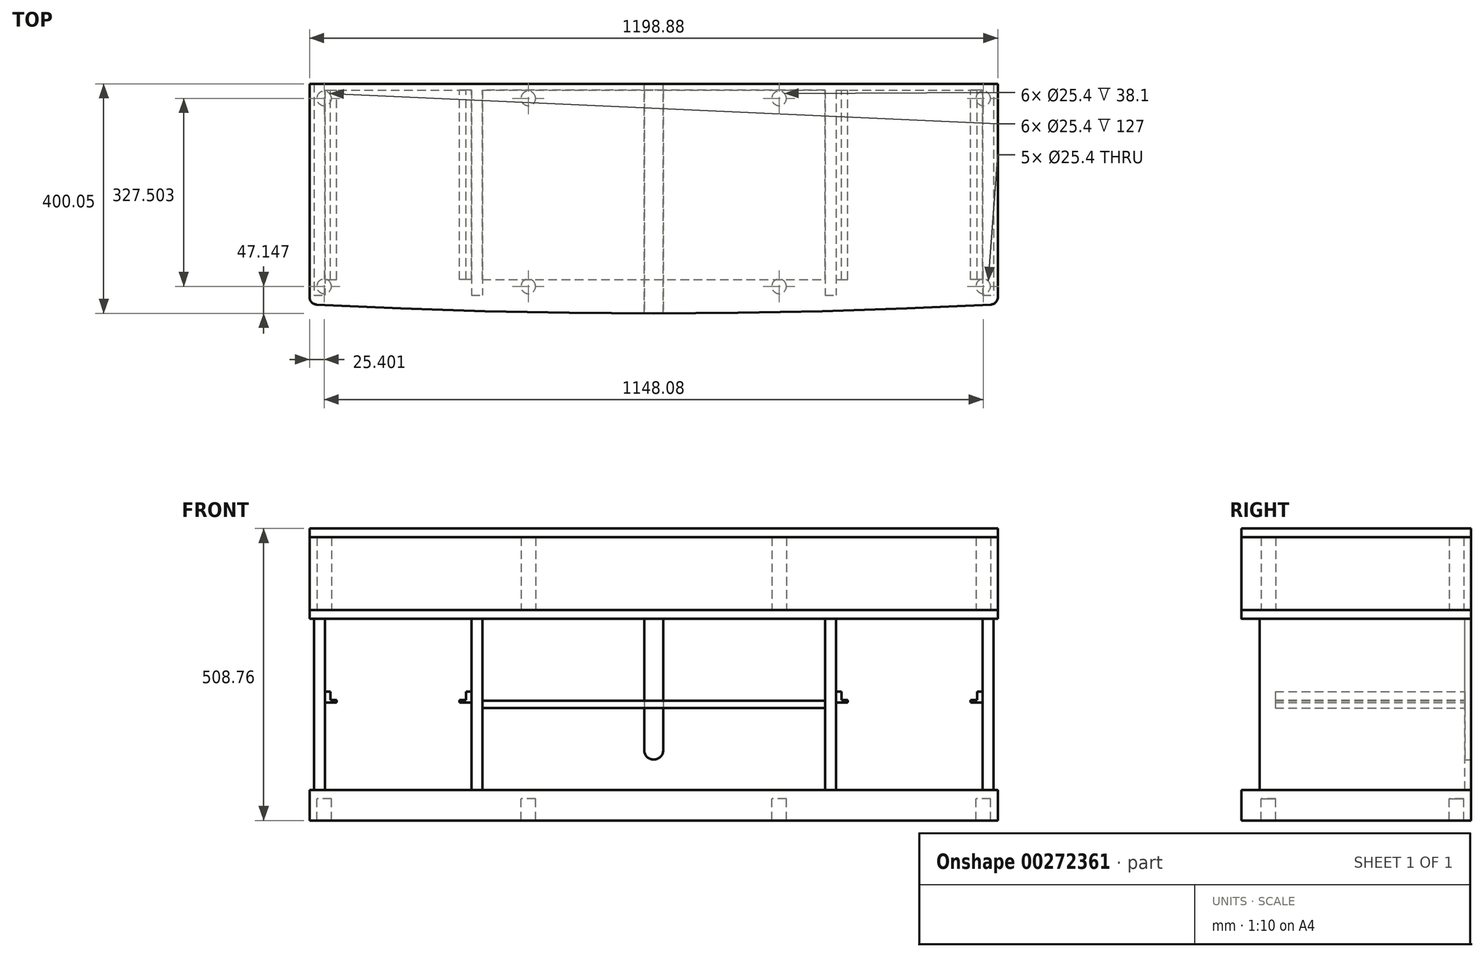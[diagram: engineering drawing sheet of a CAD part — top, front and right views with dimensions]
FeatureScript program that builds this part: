
annotation { "Feature Type Name" : "Feature", "Feature Type Description" : "" }
export const myFeature = defineFeature(function(context is Context, id is Id, definition is map)
    precondition{}
    {
        {
            var Q0;
            Q0=qCreatedBy(makeId("Top.planeOp"),FACE);
            var sketch = newSketch(context, id + "F0", { "sketchPlane" : qUnion([Q0])});
            skLineSegment(sketch, "E0.bottom", {"start": v(-605.75, 224.13) * mm, "end": v(593.13, 224.13) * mm});
            skLineSegment(sketch, "E0.left", {"start": v(-605.75, 224.13) * mm, "end": v(-605.75, -147.84) * mm});
            skLineSegment(sketch, "E0.right", {"start": v(593.13, 224.13) * mm, "end": v(593.13, -147.84) * mm});
            skLineSegment(sketch, "E1", {"start": v(-6.3, 224.13) * mm, "end": v(-6.3, -175.92) * mm, "construction": true});
            skPoint(sketch, "E2.orphan", {"position": v(593.13, -175.92) * mm});
            skPoint(sketch, "E3.orphan", {"position": v(-605.75, -175.92) * mm});
            skArc(sketch, "E4", {"start": v(-593.71, -160.52) * mm, "mid": v(-6.3, -175.92) * mm, "end": v(581.1, -160.52) * mm});
            skPoint(sketch, "E5.end.orphan", {"position": v(-592.37, -175.92) * mm});
            skPoint(sketch, "E6.MirrorCS.end.orphan", {"position": v(579.75, -175.92) * mm});
            skArc(sketch, "E7", {"start": v(-605.75, -147.84) * mm, "mid": v(-602.26, -156.58) * mm, "end": v(-593.71, -160.52) * mm});
            skPoint(sketch, "E8.orphan", {"position": v(-605.75, -159.88) * mm});
            skArc(sketch, "E9.MirrorCS", {"start": v(593.13, -147.84) * mm, "mid": v(589.64, -156.58) * mm, "end": v(581.1, -160.52) * mm});
            skPoint(sketch, "E10.orphan", {"position": v(593.13, -159.88) * mm});
            skSolve(sketch);
        }
        {
            var Q0;
            Q0=makeQuery(id+"F0.imprint","IMPRINT",FACE,{"disambiguationData":[TD([[makeQuery(id+"F0.imprint","IMPRINT",EDGE,{"derivedFrom":sQuery(id+"F0.wireOp",EDGE,"E0.bottom")}),-1.0]])]});
            extrude(context, id + "F1", {"entities" : qUnion([Q0]), "depth" : 15.24 * mm});
        }
        {
            var Q0;
            Q0=qCreatedBy(makeId("Top.planeOp"),FACE);
            cPlane(context, id + "F2", {"entities" : qUnion([Q0]), "cplaneType" : CPlaneType.OFFSET, "offset" : 63.5 * mm, "oppositeDirection" : true, "width" : 152.4 * mm, "height" : 152.4 * mm});
        }
        {
            var Q0;
            Q0=makeQuery(id+"F1.opExtrude","SWEPT_BODY",BODY,{"disambiguationData":[OSD([sQuery(id+"F0.wireOp",EDGE,"E0.bottom"),sQuery(id+"F0.wireOp",EDGE,"E0.left"),sQuery(id+"F0.wireOp",EDGE,"E0.right"),sQuery(id+"F0.wireOp",EDGE,"E4"),sQuery(id+"F0.wireOp",EDGE,"E7"),sQuery(id+"F0.wireOp",EDGE,"E9.MirrorCS")])]});
            var Q1;
            Q1=qCreatedBy(id+"F2.planeOp",FACE);
            mirror(context, id + "F3", {"entities" : qUnion([Q0]), "mirrorPlane" : qUnion([Q1])});
        }
        {
            var Q0;
            Q0=makeQuery(id+"F3.opPattern","COPY",FACE,{"derivedFrom":makeQuery(id+"F1.opExtrude","CAP_FACE",FACE,{"disambiguationData":[OSD([sQuery(id+"F0.wireOp",EDGE,"E0.bottom"),sQuery(id+"F0.wireOp",EDGE,"E0.left"),sQuery(id+"F0.wireOp",EDGE,"E0.right"),sQuery(id+"F0.wireOp",EDGE,"E4"),sQuery(id+"F0.wireOp",EDGE,"E7"),sQuery(id+"F0.wireOp",EDGE,"E9.MirrorCS")])],"isStart":true}),"instanceName":"1"});
            var sketch = newSketch(context, id + "F4", { "sketchPlane" : qUnion([Q0])});
            skCircle(sketch, "E11", {"center": v(-580.35, -128.77) * mm, "radius": 12.7 * mm});
            skCircle(sketch, "E12.MirrorC", {"center": v(567.73, -128.77) * mm, "radius": 12.7 * mm});
            skCircle(sketch, "E13.MirrorC", {"center": v(-580.35, 198.73) * mm, "radius": 12.7 * mm});
            skCircle(sketch, "E14.MirrorC", {"center": v(567.73, 198.73) * mm, "radius": 12.7 * mm});
            skLineSegment(sketch, "E15", {"start": v(-605.75, 38.15) * mm, "end": v(593.13, 38.15) * mm, "construction": true});
            skCircle(sketch, "E16", {"center": v(-224.75, 198.73) * mm, "radius": 12.7 * mm});
            skCircle(sketch, "E17.MirrorC", {"center": v(212.13, 198.73) * mm, "radius": 12.7 * mm});
            skCircle(sketch, "E18.MirrorC", {"center": v(212.13, -128.77) * mm, "radius": 12.7 * mm});
            skLineSegment(sketch, "E19", {"start": v(-580.35, -128.77) * mm, "end": v(567.73, -128.77) * mm, "construction": true});
            skLineSegment(sketch, "E20", {"start": v(-224.75, 198.73) * mm, "end": v(-224.75, -211.27) * mm, "construction": true});
            skLineSegment(sketch, "E21", {"start": v(212.13, 198.73) * mm, "end": v(212.13, -214.73) * mm, "construction": true});
            skCircle(sketch, "E22", {"center": v(-224.75, -128.77) * mm, "radius": 12.7 * mm});
            skSolve(sketch);
        }
        {
            var Q0;
            Q0=makeQuery(id+"F4.imprint","IMPRINT",FACE,{"disambiguationData":[TD([[makeQuery(id+"F4.imprint","IMPRINT",EDGE,{"derivedFrom":sQuery(id+"F4.wireOp",EDGE,"E11")}),1.0]])]});
            var Q1;
            Q1=makeQuery(id+"F4.imprint","IMPRINT",FACE,{"disambiguationData":[TD([[makeQuery(id+"F4.imprint","IMPRINT",EDGE,{"derivedFrom":sQuery(id+"F4.wireOp",EDGE,"E13.MirrorC")}),-1.0]])]});
            var Q2;
            Q2=makeQuery(id+"F4.imprint","IMPRINT",FACE,{"disambiguationData":[TD([[makeQuery(id+"F4.imprint","IMPRINT",EDGE,{"derivedFrom":sQuery(id+"F4.wireOp",EDGE,"E14.MirrorC")}),1.0]])]});
            var Q3;
            Q3=makeQuery(id+"F4.imprint","IMPRINT",FACE,{"disambiguationData":[TD([[makeQuery(id+"F4.imprint","IMPRINT",EDGE,{"derivedFrom":sQuery(id+"F4.wireOp",EDGE,"E12.MirrorC")}),-1.0]])]});
            extrude(context, id + "F5", {"entities" : qUnion([Q0, Q1, Q2, Q3]), "depth" : 127 * mm});
        }
        {
            var Q0;
            Q0=makeQuery(id+"F3.opPattern","COPY",FACE,{"derivedFrom":makeQuery(id+"F1.opExtrude","CAP_FACE",FACE,{"disambiguationData":[OSD([sQuery(id+"F0.wireOp",EDGE,"E0.bottom"),sQuery(id+"F0.wireOp",EDGE,"E0.left"),sQuery(id+"F0.wireOp",EDGE,"E0.right"),sQuery(id+"F0.wireOp",EDGE,"E4"),sQuery(id+"F0.wireOp",EDGE,"E7"),sQuery(id+"F0.wireOp",EDGE,"E9.MirrorCS")])],"isStart":false}),"instanceName":"1"});
            cPlane(context, id + "F6", {"entities" : qUnion([Q0]), "cplaneType" : CPlaneType.OFFSET, "offset" : 148.97 * mm, "width" : 152.4 * mm, "height" : 152.4 * mm});
        }
        {
            var Q0;
            Q0=makeQuery(id+"F3.opPattern","COPY",BODY,{"derivedFrom":makeQuery(id+"F1.opExtrude","SWEPT_BODY",BODY,{"disambiguationData":[OSD([sQuery(id+"F0.wireOp",EDGE,"E0.bottom"),sQuery(id+"F0.wireOp",EDGE,"E0.left"),sQuery(id+"F0.wireOp",EDGE,"E0.right"),sQuery(id+"F0.wireOp",EDGE,"E4"),sQuery(id+"F0.wireOp",EDGE,"E7"),sQuery(id+"F0.wireOp",EDGE,"E9.MirrorCS")])]}),"instanceName":"1"});
            var Q1;
            Q1=qCreatedBy(id+"F6.planeOp",FACE);
            mirror(context, id + "F7", {"entities" : qUnion([Q0]), "mirrorPlane" : qUnion([Q1])});
        }
        {
            var Q0;
            Q0=makeQuery(id+"F7.opPattern","COPY",FACE,{"derivedFrom":makeQuery(id+"F3.opPattern","COPY",FACE,{"derivedFrom":makeQuery(id+"F1.opExtrude","CAP_FACE",FACE,{"disambiguationData":[OSD([sQuery(id+"F0.wireOp",EDGE,"E0.bottom"),sQuery(id+"F0.wireOp",EDGE,"E0.left"),sQuery(id+"F0.wireOp",EDGE,"E0.right"),sQuery(id+"F0.wireOp",EDGE,"E4"),sQuery(id+"F0.wireOp",EDGE,"E7"),sQuery(id+"F0.wireOp",EDGE,"E9.MirrorCS")])],"isStart":false}),"instanceName":"1"}),"instanceName":"1"});
            var sketch = newSketch(context, id + "F8", { "sketchPlane" : qUnion([Q0])});
            skLineSegment(sketch, "E23", {"start": v(-605.75, 224.13) * mm, "end": v(-598.13, 224.13) * mm});
            skLineSegment(sketch, "E24", {"start": v(-598.13, 224.13) * mm, "end": v(-598.13, -144.17) * mm});
            skLineSegment(sketch, "E25.0", {"start": v(-579.08, 224.13) * mm, "end": v(-579.08, -144.17) * mm});
            skLineSegment(sketch, "E26", {"start": v(-6.3, 224.13) * mm, "end": v(-6.3, -175.92) * mm, "construction": true});
            skLineSegment(sketch, "E27.MirrorCS", {"start": v(566.46, 224.13) * mm, "end": v(566.46, -144.17) * mm});
            skLineSegment(sketch, "E28.MirrorCS", {"start": v(585.51, 224.13) * mm, "end": v(585.51, -144.17) * mm});
            skLineSegment(sketch, "E29", {"start": v(566.46, -144.17) * mm, "end": v(585.51, -144.17) * mm});
            skLineSegment(sketch, "E30", {"start": v(566.46, 224.13) * mm, "end": v(585.51, 224.13) * mm});
            skLineSegment(sketch, "E31", {"start": v(-6.3, 24.1) * mm, "end": v(-304.76, 24.1) * mm, "construction": true});
            skLineSegment(sketch, "E32", {"start": v(-6.3, 24.1) * mm, "end": v(292.14, 24.1) * mm, "construction": true});
            skLineSegment(sketch, "E33", {"start": v(292.14, 224.13) * mm, "end": v(292.14, -144.17) * mm});
            skLineSegment(sketch, "E34.MirrorCS", {"start": v(-304.76, 224.13) * mm, "end": v(-304.76, -144.17) * mm});
            skLineSegment(sketch, "E35.0", {"start": v(311.2, 224.13) * mm, "end": v(311.2, -144.17) * mm});
            skLineSegment(sketch, "E36.MirrorCS", {"start": v(-323.8, 224.13) * mm, "end": v(-323.8, -144.17) * mm});
            skLineSegment(sketch, "E37", {"start": v(-323.8, 224.13) * mm, "end": v(-304.76, 224.13) * mm});
            skLineSegment(sketch, "E38", {"start": v(-323.8, -144.17) * mm, "end": v(-304.76, -144.17) * mm});
            skLineSegment(sketch, "E39", {"start": v(292.14, -144.17) * mm, "end": v(311.2, -144.17) * mm});
            skLineSegment(sketch, "E40", {"start": v(292.14, 224.13) * mm, "end": v(311.2, 224.13) * mm});
            skLineSegment(sketch, "E41", {"start": v(-598.13, -144.17) * mm, "end": v(-579.08, -144.17) * mm});
            skSolve(sketch);
        }
        {
            var Q0;
            Q0=makeQuery(id+"F8.imprint","IMPRINT",FACE,{"disambiguationData":[TD([[makeQuery(id+"F8.imprint","IMPRINT",EDGE,{"derivedFrom":sQuery(id+"F8.wireOp",EDGE,"E34.MirrorCS")}),-1.0]])]});
            var Q1;
            {var subQ0=sQuery(id+"F8.wireOp",EDGE,"E24");Q1=makeQuery(id+"F8.imprint","IMPRINT",FACE,{"disambiguationData":[TD([[makeQuery(id+"F8.imprint","IMPRINT",EDGE,{"derivedFrom":subQ0}),1.0]])]});}
            var Q2;
            Q2=makeQuery(id+"F8.imprint","IMPRINT",FACE,{"disambiguationData":[TD([[makeQuery(id+"F8.imprint","IMPRINT",EDGE,{"derivedFrom":sQuery(id+"F8.wireOp",EDGE,"E33")}),1.0]])]});
            var Q3;
            Q3=makeQuery(id+"F8.imprint","IMPRINT",FACE,{"disambiguationData":[TD([[makeQuery(id+"F8.imprint","IMPRINT",EDGE,{"derivedFrom":sQuery(id+"F8.wireOp",EDGE,"E27.MirrorCS")}),1.0]])]});
            extrude(context, id + "F9", {"entities" : qUnion([Q0, Q1, Q2, Q3]), "depth" : 297.94 * mm});
        }
        {
            var Q0;
            Q0=makeQuery(id+"F5.opExtrude","SWEPT_BODY",BODY,{"disambiguationData":[OSD([sQuery(id+"F4.wireOp",EDGE,"E12.MirrorC")])]});
            var Q1;
            Q1=makeQuery(id+"F5.opExtrude","SWEPT_BODY",BODY,{"disambiguationData":[OSD([sQuery(id+"F4.wireOp",EDGE,"E14.MirrorC")])]});
            var Q2;
            Q2=makeQuery(id+"F5.opExtrude","SWEPT_BODY",BODY,{"disambiguationData":[OSD([sQuery(id+"F4.wireOp",EDGE,"E13.MirrorC")])]});
            var Q3;
            Q3=makeQuery(id+"F5.opExtrude","SWEPT_BODY",BODY,{"disambiguationData":[OSD([sQuery(id+"F4.wireOp",EDGE,"E11")])]});
            var Q4;
            Q4=qCreatedBy(id+"F6.planeOp",FACE);
            mirror(context, id + "F10", {"operationType" : NewBodyOperationType.ADD, "entities" : qUnion([Q0, Q1, Q2, Q3]), "mirrorPlane" : qUnion([Q4])});
        }
        {
            var Q0;
            Q0=makeQuery(id+"F10.opPattern","COPY",FACE,{"derivedFrom":makeQuery(id+"F5.opExtrude","CAP_FACE",FACE,{"disambiguationData":[OSD([sQuery(id+"F4.wireOp",EDGE,"E12.MirrorC")])],"isStart":false}),"instanceName":"1"});
            var Q1;
            Q1=makeQuery(id+"F10.opPattern","COPY",FACE,{"derivedFrom":makeQuery(id+"F5.opExtrude","CAP_FACE",FACE,{"disambiguationData":[OSD([sQuery(id+"F4.wireOp",EDGE,"E14.MirrorC")])],"isStart":false}),"instanceName":"1"});
            var Q2;
            Q2=makeQuery(id+"F10.opPattern","COPY",FACE,{"derivedFrom":makeQuery(id+"F5.opExtrude","CAP_FACE",FACE,{"disambiguationData":[OSD([sQuery(id+"F4.wireOp",EDGE,"E13.MirrorC")])],"isStart":false}),"instanceName":"1"});
            var Q3;
            Q3=makeQuery(id+"F10.opPattern","COPY",FACE,{"derivedFrom":makeQuery(id+"F5.opExtrude","CAP_FACE",FACE,{"disambiguationData":[OSD([sQuery(id+"F4.wireOp",EDGE,"E11")])],"isStart":false}),"instanceName":"1"});
            extrude(context, id + "F11", {"entities" : qUnion([Q0, Q1, Q2, Q3]), "operationType" : NewBodyOperationType.REMOVE, "oppositeDirection" : true, "depth" : 88.9 * mm});
        }
        {
            var Q0;
            Q0=makeQuery(id+"F7.opPattern","COPY",FACE,{"derivedFrom":makeQuery(id+"F3.opPattern","COPY",FACE,{"derivedFrom":makeQuery(id+"F1.opExtrude","CAP_FACE",FACE,{"disambiguationData":[OSD([sQuery(id+"F0.wireOp",EDGE,"E0.bottom"),sQuery(id+"F0.wireOp",EDGE,"E0.left"),sQuery(id+"F0.wireOp",EDGE,"E0.right"),sQuery(id+"F0.wireOp",EDGE,"E4"),sQuery(id+"F0.wireOp",EDGE,"E7"),sQuery(id+"F0.wireOp",EDGE,"E9.MirrorCS")])],"isStart":true}),"instanceName":"1"}),"instanceName":"1"});
            var sketch = newSketch(context, id + "F12", { "sketchPlane" : qUnion([Q0])});
            skLineSegment(sketch, "E42", {"start": v(-6.3, 175.92) * mm, "end": v(-6.3, -224.13) * mm, "construction": true});
            skCircle(sketch, "E43", {"center": v(-196.8, 148.86) * mm, "radius": 12.7 * mm});
            skCircle(sketch, "E44.MirrorC", {"center": v(184.2, 148.86) * mm, "radius": 12.7 * mm});
            skLineSegment(sketch, "E45", {"start": v(-580.35, -198.73) * mm, "end": v(567.73, -198.73) * mm, "construction": true});
            skCircle(sketch, "E46", {"center": v(-196.8, -198.73) * mm, "radius": 12.7 * mm});
            skCircle(sketch, "E47.MirrorC", {"center": v(184.2, -198.73) * mm, "radius": 12.7 * mm});
            skSolve(sketch);
        }
        {
            var Q0;
            Q0=makeQuery(id+"F12.imprint","IMPRINT",FACE,{"disambiguationData":[TD([[makeQuery(id+"F12.imprint","IMPRINT",EDGE,{"derivedFrom":sQuery(id+"F12.wireOp",EDGE,"E44.MirrorC")}),-1.0]])]});
            var Q1;
            Q1=makeQuery(id+"F12.imprint","IMPRINT",FACE,{"disambiguationData":[TD([[makeQuery(id+"F12.imprint","IMPRINT",EDGE,{"derivedFrom":sQuery(id+"F12.wireOp",EDGE,"E43")}),1.0]])]});
            var Q2;
            Q2=makeQuery(id+"F12.imprint","IMPRINT",FACE,{"disambiguationData":[TD([[makeQuery(id+"F12.imprint","IMPRINT",EDGE,{"derivedFrom":sQuery(id+"F12.wireOp",EDGE,"E47.MirrorC")}),-1.0]])]});
            var Q3;
            Q3=makeQuery(id+"F12.imprint","IMPRINT",FACE,{"disambiguationData":[TD([[makeQuery(id+"F12.imprint","IMPRINT",EDGE,{"derivedFrom":sQuery(id+"F12.wireOp",EDGE,"E46")}),1.0]])]});
            extrude(context, id + "F13", {"entities" : qUnion([Q0, Q1, Q2, Q3]), "operationType" : NewBodyOperationType.ADD, "depth" : 38.1 * mm});
        }
        {
            var Q0;
            Q0=makeQuery(id+"F4.imprint","IMPRINT",FACE,{"disambiguationData":[TD([[makeQuery(id+"F4.imprint","IMPRINT",EDGE,{"derivedFrom":sQuery(id+"F4.wireOp",EDGE,"E22")}),1.0]])]});
            var Q1;
            Q1=makeQuery(id+"F4.imprint","IMPRINT",FACE,{"disambiguationData":[TD([[makeQuery(id+"F4.imprint","IMPRINT",EDGE,{"derivedFrom":sQuery(id+"F4.wireOp",EDGE,"E18.MirrorC")}),1.0]])]});
            var Q2;
            Q2=makeQuery(id+"F4.imprint","IMPRINT",FACE,{"disambiguationData":[TD([[makeQuery(id+"F4.imprint","IMPRINT",EDGE,{"derivedFrom":sQuery(id+"F4.wireOp",EDGE,"E17.MirrorC")}),-1.0]])]});
            var Q3;
            Q3=makeQuery(id+"F4.imprint","IMPRINT",FACE,{"disambiguationData":[TD([[makeQuery(id+"F4.imprint","IMPRINT",EDGE,{"derivedFrom":sQuery(id+"F4.wireOp",EDGE,"E16")}),1.0]])]});
            extrude(context, id + "F14", {"entities" : qUnion([Q0, Q1, Q2, Q3]), "depth" : 127 * mm});
        }
        {
            var Q0;
            Q0=makeQuery(id+"F9.opExtrude","SWEPT_FACE",FACE,{"disambiguationData":[OSD([sQuery(id+"F8.wireOp",EDGE,"E30")])]});
            var sketch = newSketch(context, id + "F15", { "sketchPlane" : qUnion([Q0])});
            skLineSegment(sketch, "E48", {"start": v(-585.51, -193.4) * mm, "end": v(-574.4, -193.4) * mm, "construction": true});
            skLineSegment(sketch, "E49", {"start": v(-574.4, -142.24) * mm, "end": v(-574.4, -134.3) * mm});
            skLineSegment(sketch, "E50.bottom", {"start": v(-574.4, -134.3) * mm, "end": v(587.02, -134.3) * mm});
            skLineSegment(sketch, "E50.top", {"start": v(-574.4, -448.12) * mm, "end": v(587.02, -448.12) * mm});
            skLineSegment(sketch, "E50.left", {"start": v(-574.4, -134.3) * mm, "end": v(-574.4, -448.12) * mm});
            skLineSegment(sketch, "E50.right", {"start": v(587.02, -134.3) * mm, "end": v(587.02, -448.12) * mm});
            skLineSegment(sketch, "E51", {"start": v(-574.4, -440.18) * mm, "end": v(-574.4, -448.12) * mm});
            skLineSegment(sketch, "E52", {"start": v(598.13, -400.55) * mm, "end": v(587.02, -400.55) * mm, "construction": true});
            skLineSegment(sketch, "E53", {"start": v(587.02, -400.55) * mm, "end": v(587.02, -458.48) * mm, "construction": true});
            skSolve(sketch);
        }
        {
            var Q0;
            {var subQ1=sQuery(id+"F15.wireOp",EDGE,"E50.bottom");Q0=makeQuery(id+"F15.imprint","IMPRINT",FACE,{"disambiguationData":[TD([[makeQuery(id+"F15.imprint","IMPRINT",EDGE,{"derivedFrom":subQ1}),-1.0]])]});}
            var Q1;
            {var subQ1=sQuery(id+"F8.wireOp",EDGE,"E30");var subQ6=makeQuery(id+"F9.opExtrude","SWEPT_EDGE",EDGE,{"disambiguationData":[OSD([sQuery(id+"F0.wireOp",EDGE,"E0.bottom"),sQuery(id+"F8.wireOp",EDGE,"E27.MirrorCS"),subQ1])]});Q1=makeQuery(id+"F15.imprint","IMPRINT",FACE,{"disambiguationData":[TD([[makeQuery(id+"F15.imprint","IMPRINT",EDGE,{"derivedFrom":subQ6}),-1.0]])]});}
            extrude(context, id + "F16", {"entities" : qUnion([Q0, Q1]), "operationType" : NewBodyOperationType.REMOVE, "oppositeDirection" : true, "depth" : 11.1 * mm});
        }
        {
            var Q0;
            {var subQ1=sQuery(id+"F15.wireOp",EDGE,"E50.bottom");Q0=makeQuery(id+"F15.imprint","IMPRINT",FACE,{"disambiguationData":[TD([[makeQuery(id+"F15.imprint","IMPRINT",EDGE,{"derivedFrom":subQ1}),-1.0]])]});}
            var Q1;
            {var subQ1=sQuery(id+"F8.wireOp",EDGE,"E30");var subQ6=makeQuery(id+"F9.opExtrude","SWEPT_EDGE",EDGE,{"disambiguationData":[OSD([sQuery(id+"F0.wireOp",EDGE,"E0.bottom"),sQuery(id+"F8.wireOp",EDGE,"E27.MirrorCS"),subQ1])]});Q1=makeQuery(id+"F15.imprint","IMPRINT",FACE,{"disambiguationData":[TD([[makeQuery(id+"F15.imprint","IMPRINT",EDGE,{"derivedFrom":subQ6}),-1.0]])]});}
            extrude(context, id + "F17", {"entities" : qUnion([Q0, Q1]), "operationType" : NewBodyOperationType.ADD, "oppositeDirection" : true, "depth" : 11.1 * mm});
        }
        {
            var Q0;
            {var subQ0=sQuery(id+"F0.wireOp",EDGE,"E0.bottom");var subQ1=makeQuery(id+"F3.opPattern","COPY",FACE,{"derivedFrom":makeQuery(id+"F1.opExtrude","SWEPT_FACE",FACE,{"disambiguationData":[OSD([subQ0])]}),"instanceName":"1"});Q0=makeQuery(id+"F17.boolean.opBoolean","MERGE",FACE,{"derivedFrom":[subQ1,makeQuery(id+"F7.opPattern","COPY",FACE,{"derivedFrom":subQ1,"instanceName":"1"}),makeQuery(id+"F9.opExtrude","SWEPT_FACE",FACE,{"disambiguationData":[OSD([sQuery(id+"F8.wireOp",EDGE,"E30")])]}),makeQuery(id+"F9.opExtrude","SWEPT_FACE",FACE,{"disambiguationData":[OSD([subQ0])]}),makeQuery(id+"F17.opExtrude","CAP_FACE",FACE,{"disambiguationData":[OSD([sQuery(id+"F15.wireOp",EDGE,"E50.bottom"),sQuery(id+"F15.wireOp",EDGE,"E50.top"),sQuery(id+"F15.wireOp",EDGE,"E50.left"),sQuery(id+"F15.wireOp",EDGE,"E50.right"),sQuery(id+"F15.wireOp",EDGE,"E51")])],"isStart":true})]});}
            var sketch = newSketch(context, id + "F18", { "sketchPlane" : qUnion([Q0])});
            skLineSegment(sketch, "E54", {"start": v(-292.16, -142.22) * mm, "end": v(304.74, -142.22) * mm, "construction": true});
            skLineSegment(sketch, "E55.left", {"start": v(22.96, -370.82) * mm, "end": v(22.96, -142.22) * mm});
            skLineSegment(sketch, "E55.right", {"start": v(-10.38, -370.82) * mm, "end": v(-10.38, -142.22) * mm});
            skPoint(sketch, "E55.middle", {"position": v(6.29, -142.22) * mm});
            skArc(sketch, "E56", {"start": v(-10.38, -370.82) * mm, "mid": v(6.29, -387.5) * mm, "end": v(22.96, -370.82) * mm});
            skPoint(sketch, "E55.top.end.orphan", {"position": v(-10.38, 86.38) * mm});
            skPoint(sketch, "E57.orphan", {"position": v(22.96, 86.38) * mm});
            skLineSegment(sketch, "E58", {"start": v(-10.38, -142.22) * mm, "end": v(22.96, -142.22) * mm});
            skSolve(sketch);
        }
        {
            var Q0;
            Q0=makeQuery(id+"F18.imprint","IMPRINT",FACE,{"disambiguationData":[TD([[makeQuery(id+"F18.imprint","IMPRINT",EDGE,{"derivedFrom":sQuery(id+"F18.wireOp",EDGE,"E55.left")}),1.0]])]});
            extrude(context, id + "F19", {"entities" : qUnion([Q0]), "operationType" : NewBodyOperationType.REMOVE, "endBound" : BoundingType.UP_TO_NEXT, "oppositeDirection" : true, "depth" : 25.4 * mm});
        }
        {
            var Q0;
            Q0=makeQuery(id+"F9.opExtrude","SWEPT_FACE",FACE,{"disambiguationData":[OSD([sQuery(id+"F8.wireOp",EDGE,"E33")])]});
            var sketch = newSketch(context, id + "F20", { "sketchPlane" : qUnion([Q0])});
            skLineSegment(sketch, "E59", {"start": v(-33.63, -440.18) * mm, "end": v(-33.63, -142.24) * mm, "construction": true});
            skLineSegment(sketch, "E60", {"start": v(-33.63, -291.21) * mm, "end": v(-213.02, -291.21) * mm, "construction": true});
            skLineSegment(sketch, "E61.bottom", {"start": v(117.18, -284.86) * mm, "end": v(-213.02, -284.86) * mm});
            skLineSegment(sketch, "E61.top", {"start": v(117.18, -297.56) * mm, "end": v(-213.02, -297.56) * mm});
            skLineSegment(sketch, "E61.left", {"start": v(117.18, -284.86) * mm, "end": v(117.18, -297.56) * mm});
            skLineSegment(sketch, "E61.right", {"start": v(-213.02, -284.86) * mm, "end": v(-213.02, -297.56) * mm});
            skPoint(sketch, "E61.middle", {"position": v(-47.92, -291.21) * mm});
            skSolve(sketch);
        }
        {
            var Q0;
            Q0=makeQuery(id+"F20.imprint","IMPRINT",FACE,{"disambiguationData":[TD([[makeQuery(id+"F20.imprint","IMPRINT",EDGE,{"derivedFrom":sQuery(id+"F20.wireOp",EDGE,"E61.bottom")}),1.0]])]});
            extrude(context, id + "F21", {"entities" : qUnion([Q0]), "operationType" : NewBodyOperationType.ADD, "depth" : 596.9 * mm});
        }
        {
            var Q0;
            Q0=makeQuery(id+"F17.boolean.opBoolean","SPLIT",FACE,{"disambiguationData":[TD([makeQuery(id+"F9.opExtrude","SWEPT_FACE",FACE,{"disambiguationData":[OSD([sQuery(id+"F8.wireOp",EDGE,"E25.0")])]})])],"derivedFrom":makeQuery(id+"F17.opExtrude","CAP_FACE",FACE,{"disambiguationData":[OSD([sQuery(id+"F15.wireOp",EDGE,"E50.bottom"),sQuery(id+"F15.wireOp",EDGE,"E50.top"),sQuery(id+"F15.wireOp",EDGE,"E50.left"),sQuery(id+"F15.wireOp",EDGE,"E50.right"),sQuery(id+"F15.wireOp",EDGE,"E51")])],"isStart":false})});
            var sketch = newSketch(context, id + "F22", { "sketchPlane" : qUnion([Q0])});
            skLineSegment(sketch, "E62", {"start": v(-451.44, -142.24) * mm, "end": v(-451.44, -440.18) * mm, "construction": true});
            skSolve(sketch);
        }
        {
            var Q0;
            {var subQ0=sQuery(id+"F15.wireOp",EDGE,"E51");var subQ1=sQuery(id+"F15.wireOp",EDGE,"E50.right");var subQ2=sQuery(id+"F15.wireOp",EDGE,"E50.left");var subQ3=sQuery(id+"F15.wireOp",EDGE,"E50.top");var subQ4=sQuery(id+"F15.wireOp",EDGE,"E50.bottom");var subQ5=makeQuery(id+"F16.opExtrude","CAP_FACE",FACE,{"disambiguationData":[OSD([subQ4,subQ3,subQ2,subQ1,subQ0])],"isStart":false});var subQ6=makeQuery(id+"F9.opExtrude","SWEPT_FACE",FACE,{"disambiguationData":[OSD([sQuery(id+"F8.wireOp",EDGE,"E25.0")])]});Q0=makeQuery(id+"F22.imprint","IMPRINT",FACE,{"disambiguationData":[TD([[makeQuery(id+"F22.imprint","IMPRINT",EDGE,{"derivedFrom":makeQuery(id+"F16.boolean.opBoolean","INTERSECT",EDGE,{"derivedFrom":[subQ6,subQ5]})}),-1.0]])]});}
            var sketch = newSketch(context, id + "F23", { "sketchPlane" : qUnion([Q0])});
            skLineSegment(sketch, "E63.bottom", {"start": v(-323.74, -269.24) * mm, "end": v(-333.26, -269.24) * mm});
            skLineSegment(sketch, "E63.top", {"start": v(-323.74, -288.3) * mm, "end": v(-344.38, -288.3) * mm});
            skLineSegment(sketch, "E63.left", {"start": v(-323.74, -269.24) * mm, "end": v(-323.74, -288.3) * mm});
            skLineSegment(sketch, "E63.right", {"start": v(-344.38, -283.53) * mm, "end": v(-344.38, -288.3) * mm});
            skLineSegment(sketch, "E64", {"start": v(-333.26, -269.24) * mm, "end": v(-333.26, -283.53) * mm});
            skLineSegment(sketch, "E65", {"start": v(-333.26, -283.53) * mm, "end": v(-344.38, -283.53) * mm});
            skLineSegment(sketch, "E66.MirrorCS", {"start": v(-579.15, -269.24) * mm, "end": v(-569.62, -269.24) * mm});
            skLineSegment(sketch, "E67.MirrorCS", {"start": v(-569.62, -269.24) * mm, "end": v(-569.62, -283.53) * mm});
            skLineSegment(sketch, "E68.MirrorCS", {"start": v(-569.62, -283.53) * mm, "end": v(-558.51, -283.53) * mm});
            skLineSegment(sketch, "E69.MirrorCS", {"start": v(-579.15, -288.3) * mm, "end": v(-558.51, -288.3) * mm});
            skLineSegment(sketch, "E70.MirrorCS", {"start": v(-579.15, -269.24) * mm, "end": v(-579.15, -288.3) * mm});
            skLineSegment(sketch, "E71.MirrorCS", {"start": v(-558.51, -283.53) * mm, "end": v(-558.51, -288.3) * mm});
            skLineSegment(sketch, "E72", {"start": v(-6.3, 0) * mm, "end": v(-6.3, -482.33) * mm, "construction": true});
            skLineSegment(sketch, "E73.MirrorCS", {"start": v(311.12, -269.24) * mm, "end": v(320.65, -269.24) * mm});
            skLineSegment(sketch, "E74.MirrorCS", {"start": v(320.65, -269.24) * mm, "end": v(320.65, -283.53) * mm});
            skLineSegment(sketch, "E75.MirrorCS", {"start": v(311.12, -269.24) * mm, "end": v(311.12, -288.3) * mm});
            skLineSegment(sketch, "E76.MirrorCS", {"start": v(311.12, -288.29) * mm, "end": v(331.76, -288.29) * mm});
            skLineSegment(sketch, "E77.MirrorCS", {"start": v(320.65, -283.53) * mm, "end": v(331.76, -283.53) * mm});
            skLineSegment(sketch, "E78.MirrorCS", {"start": v(331.76, -283.53) * mm, "end": v(331.76, -288.29) * mm});
            skLineSegment(sketch, "E79.MirrorCS", {"start": v(566.53, -269.24) * mm, "end": v(557, -269.24) * mm});
            skLineSegment(sketch, "E80.MirrorCS", {"start": v(557, -269.24) * mm, "end": v(557, -283.53) * mm});
            skLineSegment(sketch, "E81.MirrorCS", {"start": v(557, -283.53) * mm, "end": v(545.9, -283.53) * mm});
            skLineSegment(sketch, "E82.MirrorCS", {"start": v(545.9, -283.53) * mm, "end": v(545.9, -288.29) * mm});
            skLineSegment(sketch, "E83.MirrorCS", {"start": v(566.53, -288.29) * mm, "end": v(545.9, -288.29) * mm});
            skLineSegment(sketch, "E84.MirrorCS", {"start": v(566.53, -269.24) * mm, "end": v(566.53, -288.29) * mm});
            skSolve(sketch);
        }
        {
            var Q0;
            {var subQ1=sQuery(id+"F23.wireOp",EDGE,"E63.right");Q0=makeQuery(id+"F23.imprint","IMPRINT",FACE,{"disambiguationData":[TD([[makeQuery(id+"F23.imprint","IMPRINT",EDGE,{"derivedFrom":subQ1}),1.0]])]});}
            var Q1;
            {var subQ0=sQuery(id+"F23.wireOp",EDGE,"E67.MirrorCS");Q1=makeQuery(id+"F23.imprint","IMPRINT",FACE,{"disambiguationData":[TD([[makeQuery(id+"F23.imprint","IMPRINT",EDGE,{"derivedFrom":subQ0}),-1.0]])]});}
            var Q2;
            Q2=makeQuery(id+"F23.imprint","IMPRINT",FACE,{"disambiguationData":[TD([[makeQuery(id+"F23.imprint","IMPRINT",EDGE,{"derivedFrom":sQuery(id+"F23.wireOp",EDGE,"E73.MirrorCS")}),-1.0]])]});
            var Q3;
            Q3=makeQuery(id+"F23.imprint","IMPRINT",FACE,{"disambiguationData":[TD([[makeQuery(id+"F23.imprint","IMPRINT",EDGE,{"derivedFrom":sQuery(id+"F23.wireOp",EDGE,"E79.MirrorCS")}),1.0]])]});
            extrude(context, id + "F24", {"entities" : qUnion([Q0, Q1, Q2, Q3]), "operationType" : NewBodyOperationType.ADD, "depth" : 330.2 * mm});
        }
    });
